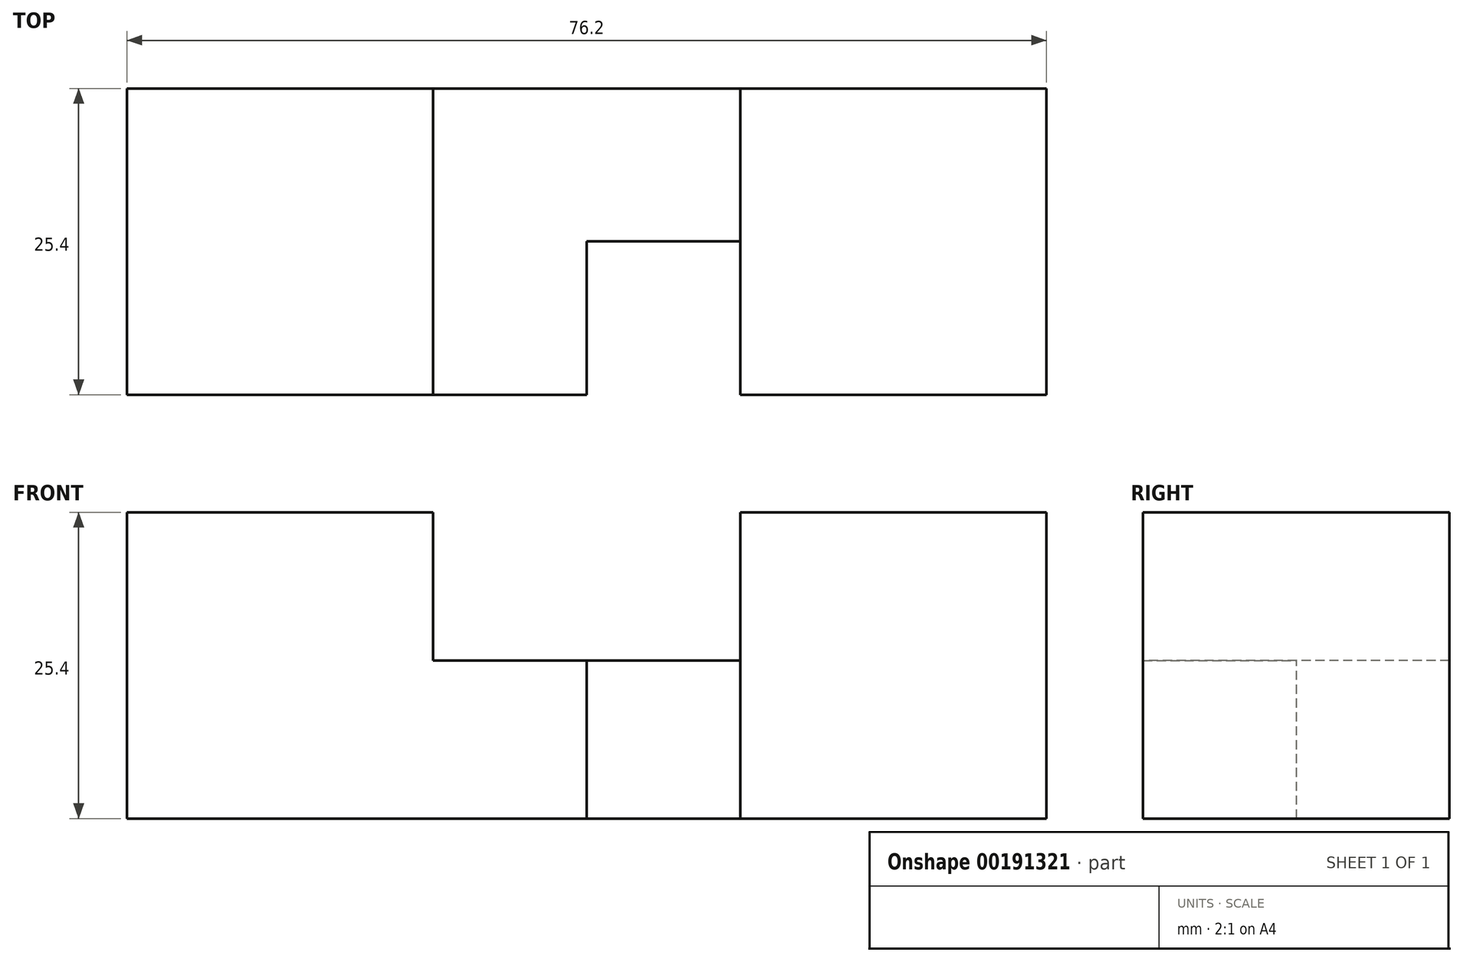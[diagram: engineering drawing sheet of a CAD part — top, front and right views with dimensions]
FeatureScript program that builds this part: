
annotation { "Feature Type Name" : "Feature", "Feature Type Description" : "" }
export const myFeature = defineFeature(function(context is Context, id is Id, definition is map)
    precondition{}
    {
        {
            var Q0;
            Q0=qCreatedBy(makeId("Top.planeOp"),FACE);
            var sketch = newSketch(context, id + "F0", { "sketchPlane" : qUnion([Q0])});
            skLineSegment(sketch, "E0.bottom", {"start": v(0, 0) * mm, "end": v(76.2, 0) * mm});
            skLineSegment(sketch, "E0.top", {"start": v(0, 25.4) * mm, "end": v(76.2, 25.4) * mm});
            skLineSegment(sketch, "E0.left", {"start": v(0, 0) * mm, "end": v(0, 25.4) * mm});
            skLineSegment(sketch, "E0.right", {"start": v(76.2, 0) * mm, "end": v(76.2, 25.4) * mm});
            skSolve(sketch);
        }
        {
            var Q0;
            Q0=makeQuery(id+"F0.imprint","IMPRINT",FACE,{"disambiguationData":[TD([[makeQuery(id+"F0.imprint","IMPRINT",EDGE,{"derivedFrom":sQuery(id+"F0.wireOp",EDGE,"E0.bottom")}),1.0]])]});
            extrude(context, id + "F1", {"entities" : qUnion([Q0]), "depth" : 25.4 * mm});
        }
        {
            var Q0;
            Q0=qCreatedBy(makeId("Front.planeOp"),FACE);
            var sketch = newSketch(context, id + "F2", { "sketchPlane" : qUnion([Q0])});
            skLineSegment(sketch, "E1.bottom", {"start": v(25.37, 25.82) * mm, "end": v(50.83, 25.82) * mm});
            skLineSegment(sketch, "E1.top", {"start": v(25.37, 13.1) * mm, "end": v(50.83, 13.1) * mm});
            skLineSegment(sketch, "E1.left", {"start": v(25.37, 25.82) * mm, "end": v(25.37, 13.1) * mm});
            skLineSegment(sketch, "E1.right", {"start": v(50.83, 25.82) * mm, "end": v(50.83, 13.1) * mm});
            skSolve(sketch);
        }
        {
            var Q0;
            Q0=makeQuery(id+"F2.imprint","IMPRINT",FACE,{"disambiguationData":[TD([[makeQuery(id+"F2.imprint","IMPRINT",EDGE,{"derivedFrom":sQuery(id+"F2.wireOp",EDGE,"E1.bottom")}),-1.0]])]});
            extrude(context, id + "F3", {"entities" : qUnion([Q0]), "operationType" : NewBodyOperationType.REMOVE, "oppositeDirection" : true, "depth" : 25.4 * mm});
        }
        {
            var Q0;
            Q0=makeQuery(id+"F3.boolean.opBoolean","COPY",FACE,{"derivedFrom":makeQuery(id+"F3.opExtrude","SWEPT_FACE",FACE,{"disambiguationData":[OSD([sQuery(id+"F2.wireOp",EDGE,"E1.top")])]})});
            var sketch = newSketch(context, id + "F4", { "sketchPlane" : qUnion([Q0])});
            skLineSegment(sketch, "E2.bottom", {"start": v(50.83, 0) * mm, "end": v(38.1, 0) * mm});
            skLineSegment(sketch, "E2.top", {"start": v(50.83, 12.73) * mm, "end": v(38.1, 12.73) * mm});
            skLineSegment(sketch, "E2.left", {"start": v(50.83, 0) * mm, "end": v(50.83, 12.73) * mm});
            skLineSegment(sketch, "E2.right", {"start": v(38.1, 0) * mm, "end": v(38.1, 12.73) * mm});
            skSolve(sketch);
        }
        {
            var Q0;
            Q0=makeQuery(id+"F4.imprint","IMPRINT",FACE,{"disambiguationData":[TD([[makeQuery(id+"F4.imprint","IMPRINT",EDGE,{"derivedFrom":sQuery(id+"F4.wireOp",EDGE,"E2.bottom")}),1.0]])]});
            extrude(context, id + "F5", {"entities" : qUnion([Q0]), "operationType" : NewBodyOperationType.REMOVE, "oppositeDirection" : true, "depth" : 25.4 * mm});
        }
    });
